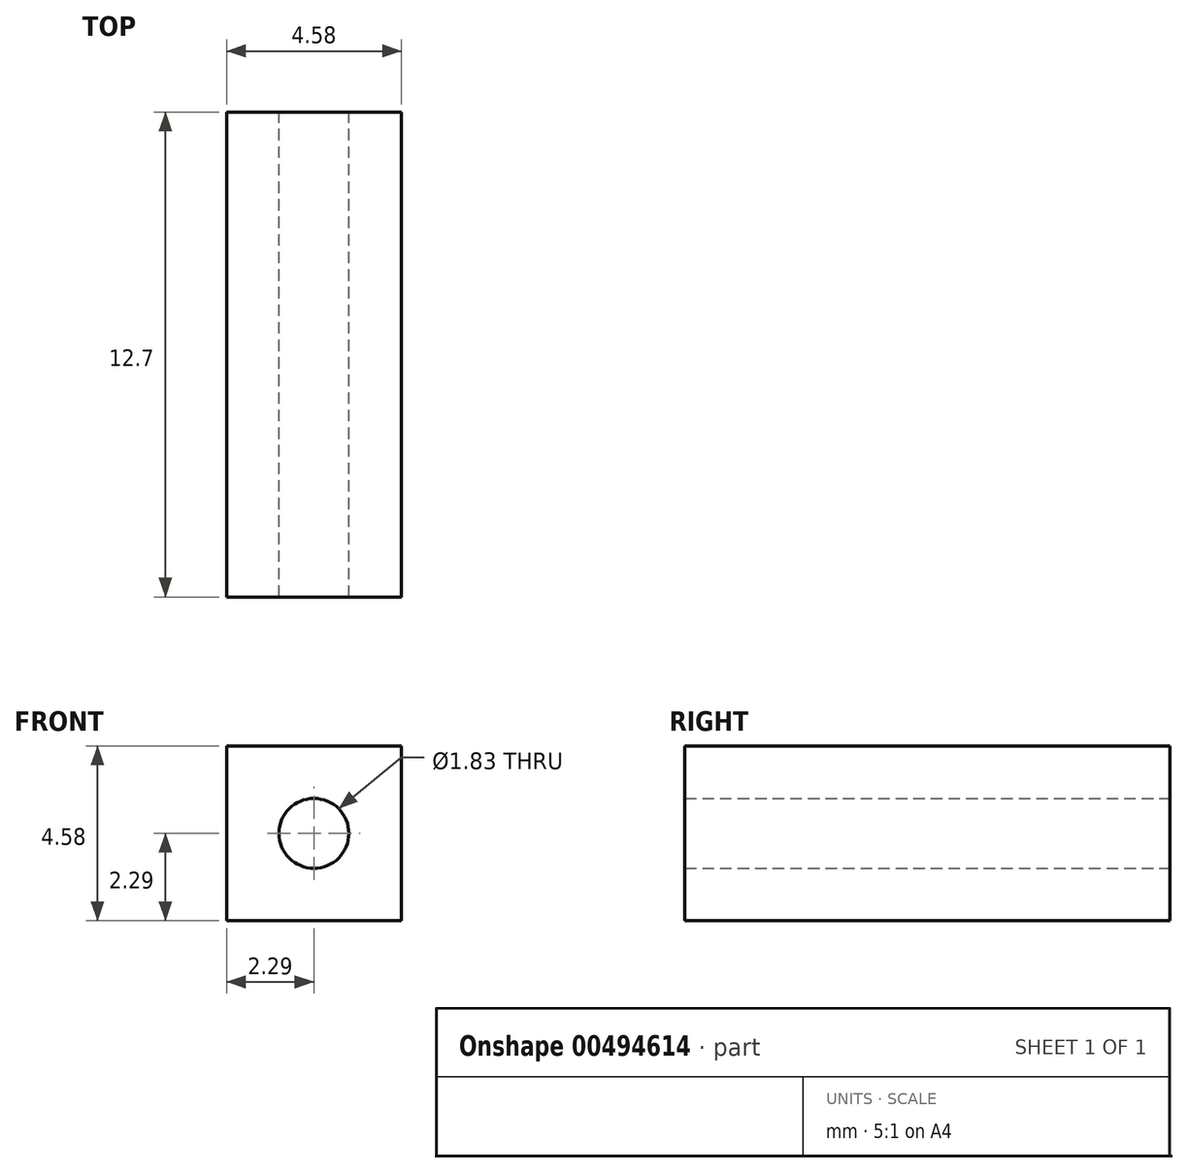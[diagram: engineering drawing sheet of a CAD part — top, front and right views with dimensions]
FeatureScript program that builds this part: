
annotation { "Feature Type Name" : "Feature", "Feature Type Description" : "" }
export const myFeature = defineFeature(function(context is Context, id is Id, definition is map)
    precondition{}
    {
        {
            var Q0;
            Q0=qCreatedBy(makeId("Front.planeOp"),FACE);
            var sketch = newSketch(context, id + "F0", { "sketchPlane" : qUnion([Q0])});
            skLineSegment(sketch, "E0.bottom", {"start": v(-2.29, 2.29) * mm, "end": v(2.29, 2.29) * mm});
            skLineSegment(sketch, "E0.top", {"start": v(-2.29, -2.29) * mm, "end": v(2.29, -2.29) * mm});
            skLineSegment(sketch, "E0.left", {"start": v(-2.29, 2.29) * mm, "end": v(-2.29, -2.29) * mm});
            skLineSegment(sketch, "E0.right", {"start": v(2.29, 2.29) * mm, "end": v(2.29, -2.29) * mm});
            skCircle(sketch, "E1", {"center": v(0, 0) * mm, "radius": 0.91 * mm});
            skSolve(sketch);
        }
        {
            var Q0;
            Q0=makeQuery(id+"F0.imprint","IMPRINT",FACE,{"disambiguationData":[TD([[makeQuery(id+"F0.imprint","IMPRINT",EDGE,{"derivedFrom":sQuery(id+"F0.wireOp",EDGE,"E0.bottom")}),-1.0]])]});
            extrude(context, id + "F1", {"entities" : qUnion([Q0]), "depth" : 12.7 * mm});
        }
    });
